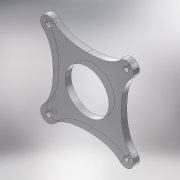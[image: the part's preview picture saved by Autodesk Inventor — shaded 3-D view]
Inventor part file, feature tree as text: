
AUTODESK INVENTOR PART (.ipt)
format: ipt  version: 2018.2 (Build 222227000, 227)  size: 169,472 bytes
history: native  units: mm
features: extrude x1, sketch x1
ambient origin geometry x8: Origin, YZ Plane, XZ Plane, XY Plane, X Axis, Y Axis, Z Axis, Center Point
bodies: Solid1 (feature_tree)
feature tree (2):
  extrude  "Extrusion1"  Depth=80.0mm
  sketch  "Sketch1"  dims[d0=80.0mm d1=80.0mm d2=5.0mm d4=45.0deg d5=5.0mm d6=45.0mm d7=8.0mm d8=6.0mm d9=0.0mm]
